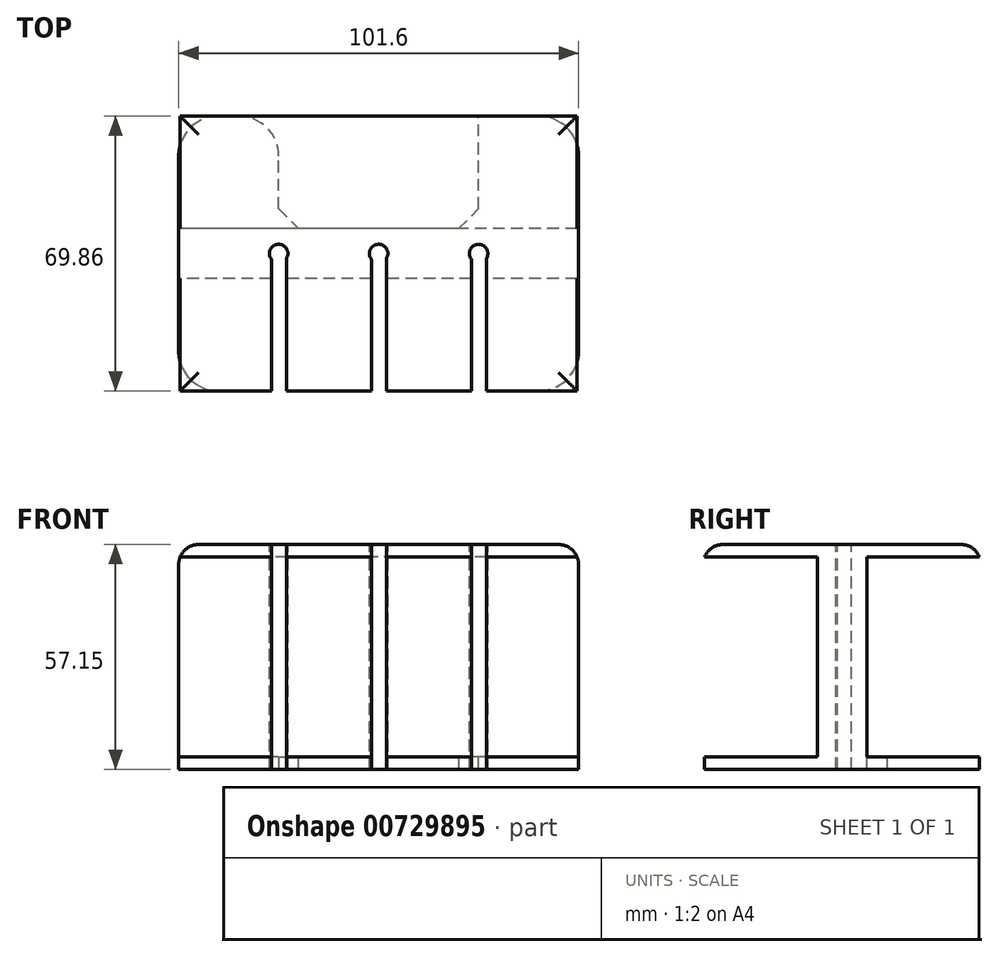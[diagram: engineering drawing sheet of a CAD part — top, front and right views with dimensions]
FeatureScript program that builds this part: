
annotation { "Feature Type Name" : "Feature", "Feature Type Description" : "" }
export const myFeature = defineFeature(function(context is Context, id is Id, definition is map)
    precondition{}
    {
        {
            var Q0;
            Q0=qCreatedBy(makeId("Right.planeOp"),FACE);
            var sketch = newSketch(context, id + "F0", { "sketchPlane" : qUnion([Q0])});
            skLineSegment(sketch, "E0.bottom", {"start": v(6.3, 28.58) * mm, "end": v(-6.3, 28.58) * mm});
            skLineSegment(sketch, "E0.top", {"start": v(6.3, -28.58) * mm, "end": v(-6.3, -28.58) * mm});
            skLineSegment(sketch, "E0.left", {"start": v(6.3, 28.58) * mm, "end": v(6.3, -28.58) * mm});
            skLineSegment(sketch, "E0.right", {"start": v(-6.3, 28.58) * mm, "end": v(-6.3, -28.58) * mm});
            skPoint(sketch, "E0.middle", {"position": v(0, 0) * mm});
            skLineSegment(sketch, "E1.bottom", {"start": v(0, 28.58) * mm, "end": v(-34.93, 28.58) * mm});
            skLineSegment(sketch, "E1.top", {"start": v(0, 25.4) * mm, "end": v(-34.93, 25.4) * mm});
            skLineSegment(sketch, "E1.left", {"start": v(0, 28.58) * mm, "end": v(0, 25.4) * mm});
            skLineSegment(sketch, "E1.right", {"start": v(-34.93, 28.57) * mm, "end": v(-34.93, 25.4) * mm});
            skLineSegment(sketch, "E2.MirrorCS", {"start": v(0, 28.58) * mm, "end": v(34.93, 28.58) * mm});
            skLineSegment(sketch, "E3.MirrorCS", {"start": v(0, 25.4) * mm, "end": v(34.93, 25.4) * mm});
            skLineSegment(sketch, "E4.MirrorCS", {"start": v(34.93, 28.58) * mm, "end": v(34.93, 25.4) * mm});
            skLineSegment(sketch, "E5.MirrorCS", {"start": v(0, -28.58) * mm, "end": v(-34.92, -28.58) * mm});
            skLineSegment(sketch, "E6.MirrorCS", {"start": v(0, -28.58) * mm, "end": v(34.93, -28.58) * mm});
            skLineSegment(sketch, "E7.MirrorCS", {"start": v(0, -25.4) * mm, "end": v(34.93, -25.4) * mm});
            skLineSegment(sketch, "E8.MirrorCS", {"start": v(0, -25.4) * mm, "end": v(-34.92, -25.4) * mm});
            skLineSegment(sketch, "E9.MirrorCS", {"start": v(-34.93, -28.58) * mm, "end": v(-34.93, -25.4) * mm});
            skLineSegment(sketch, "E10.MirrorCS", {"start": v(34.93, -28.58) * mm, "end": v(34.93, -25.4) * mm});
            skSolve(sketch);
        }
        {
            var Q0;
            Q0 = qSketchRegion(id + "F0", true);
            extrude(context, id + "F1", {"entities" : qUnion([Q0]), "endBound" : BoundingType.SYMMETRIC, "depth" : 101.6 * mm, "offsetDistance" : 25.4 * mm});
        }
        {
            var Q0;
            Q0=makeQuery(id+"F1.opExtrude","SWEPT_FACE",FACE,{"disambiguationData":[OSD([sQuery(id+"F0.wireOp",EDGE,"E1.bottom"),sQuery(id+"F0.wireOp",EDGE,"E2.MirrorCS")])]});
            fillet(context, id + "F2", {"entities" : qUnion([Q0]), "radius" : 5.08 * mm, "tangentPropagation" : true, "allowEdgeOverflow" : false});
        }
        {
            var Q0;
            Q0=makeQuery(id+"F1.opExtrude","SWEPT_FACE",FACE,{"disambiguationData":[OSD([sQuery(id+"F0.wireOp",EDGE,"E1.bottom"),sQuery(id+"F0.wireOp",EDGE,"E2.MirrorCS")])]});
            var sketch = newSketch(context, id + "F3", { "sketchPlane" : qUnion([Q0])});
            skCircle(sketch, "E11", {"center": v(0, 0) * mm, "radius": 2.35 * mm});
            skCircle(sketch, "E12", {"center": v(-25.4, 0) * mm, "radius": 2.35 * mm});
            skCircle(sketch, "E13", {"center": v(25.4, 0) * mm, "radius": 2.35 * mm});
            skLineSegment(sketch, "E14", {"start": v(-27.26, 0) * mm, "end": v(-27.26, -36.25) * mm});
            skLineSegment(sketch, "E15", {"start": v(-27.26, -36.25) * mm, "end": v(-23.45, -36.25) * mm});
            skLineSegment(sketch, "E16", {"start": v(-23.45, -36.25) * mm, "end": v(-23.45, 0) * mm});
            skLineSegment(sketch, "E17", {"start": v(-1.86, 0) * mm, "end": v(-1.86, -35.89) * mm});
            skLineSegment(sketch, "E18", {"start": v(-1.86, -35.89) * mm, "end": v(1.95, -35.89) * mm});
            skLineSegment(sketch, "E19", {"start": v(1.95, -35.89) * mm, "end": v(1.95, 0) * mm});
            skLineSegment(sketch, "E20", {"start": v(23.6, 0) * mm, "end": v(23.6, -37.47) * mm});
            skLineSegment(sketch, "E21", {"start": v(23.6, -37.47) * mm, "end": v(27.41, -37.47) * mm});
            skLineSegment(sketch, "E22", {"start": v(27.41, -37.47) * mm, "end": v(27.41, 0) * mm});
            skSolve(sketch);
        }
        {
            var Q0;
            Q0 = qSketchRegion(id + "F3", true);
            extrude(context, id + "F4", {"entities" : qUnion([Q0]), "operationType" : NewBodyOperationType.REMOVE, "endBound" : BoundingType.THROUGH_ALL, "oppositeDirection" : true, "depth" : 25.4 * mm, "offsetDistance" : 25.4 * mm});
        }
        {
            var Q0;
            Q0=makeQuery(id+"F1.opExtrude","SWEPT_FACE",FACE,{"disambiguationData":[OSD([sQuery(id+"F0.wireOp",EDGE,"E7.MirrorCS")])]});
            var sketch = newSketch(context, id + "F5", { "sketchPlane" : qUnion([Q0])});
            skLineSegment(sketch, "E23.bottom", {"start": v(-25.4, 6.3) * mm, "end": v(25.4, 6.3) * mm});
            skLineSegment(sketch, "E23.top", {"start": v(-25.4, 34.93) * mm, "end": v(25.4, 34.93) * mm});
            skLineSegment(sketch, "E23.left", {"start": v(-25.4, 6.3) * mm, "end": v(-25.4, 34.93) * mm});
            skLineSegment(sketch, "E23.right", {"start": v(25.4, 6.3) * mm, "end": v(25.4, 34.93) * mm});
            skSolve(sketch);
        }
        {
            var Q0;
            Q0 = qSketchRegion(id + "F5", true);
            extrude(context, id + "F6", {"entities" : qUnion([Q0]), "operationType" : NewBodyOperationType.REMOVE, "endBound" : BoundingType.THROUGH_ALL, "oppositeDirection" : true, "depth" : 25.4 * mm, "offsetDistance" : 25.4 * mm});
        }
        {
            var Q0;
            Q0=makeQuery(id+"F1.opExtrude","CAP_EDGE",EDGE,{"disambiguationData":[OSD([sQuery(id+"F0.wireOp",EDGE,"E10.MirrorCS")])],"isStart":false});
            var Q1;
            Q1=makeQuery(id+"F6.boolean.opBoolean","COPY",EDGE,{"derivedFrom":makeQuery(id+"F6.opExtrude","SWEPT_EDGE",EDGE,{"disambiguationData":[OSD([sQuery(id+"F0.wireOp",EDGE,"E7.MirrorCS"),sQuery(id+"F0.wireOp",EDGE,"E10.MirrorCS"),sQuery(id+"F5.wireOp",EDGE,"E23.top"),sQuery(id+"F5.wireOp",EDGE,"E23.right")])]})});
            var Q2;
            Q2=makeQuery(id+"F6.boolean.opBoolean","COPY",EDGE,{"derivedFrom":makeQuery(id+"F6.opExtrude","SWEPT_EDGE",EDGE,{"disambiguationData":[OSD([sQuery(id+"F0.wireOp",EDGE,"E7.MirrorCS"),sQuery(id+"F0.wireOp",EDGE,"E10.MirrorCS"),sQuery(id+"F5.wireOp",EDGE,"E23.top"),sQuery(id+"F5.wireOp",EDGE,"E23.left")])]})});
            var Q3;
            Q3=makeQuery(id+"F1.opExtrude","CAP_EDGE",EDGE,{"disambiguationData":[OSD([sQuery(id+"F0.wireOp",EDGE,"E10.MirrorCS")])],"isStart":true});
            var Q4;
            Q4=makeQuery(id+"F1.opExtrude","CAP_EDGE",EDGE,{"disambiguationData":[OSD([sQuery(id+"F0.wireOp",EDGE,"E9.MirrorCS")])],"isStart":true});
            var Q5;
            Q5=makeQuery(id+"F1.opExtrude","CAP_EDGE",EDGE,{"disambiguationData":[OSD([sQuery(id+"F0.wireOp",EDGE,"E9.MirrorCS")])],"isStart":false});
            fillet(context, id + "F7", {"entities" : qUnion([Q0, Q1, Q2, Q3, Q4, Q5]), "radius" : 10.16 * mm, "tangentPropagation" : true, "allowEdgeOverflow" : false});
        }
        {
            var Q0;
            Q0=makeQuery(id+"F6.boolean.opBoolean","COPY",EDGE,{"derivedFrom":makeQuery(id+"F6.opExtrude","SWEPT_EDGE",EDGE,{"disambiguationData":[OSD([sQuery(id+"F0.wireOp",EDGE,"E0.left"),sQuery(id+"F0.wireOp",EDGE,"E7.MirrorCS"),sQuery(id+"F5.wireOp",EDGE,"E23.bottom"),sQuery(id+"F5.wireOp",EDGE,"E23.left")])]})});
            var Q1;
            Q1=makeQuery(id+"F6.boolean.opBoolean","COPY",EDGE,{"derivedFrom":makeQuery(id+"F6.opExtrude","SWEPT_EDGE",EDGE,{"disambiguationData":[OSD([sQuery(id+"F0.wireOp",EDGE,"E0.left"),sQuery(id+"F0.wireOp",EDGE,"E7.MirrorCS"),sQuery(id+"F5.wireOp",EDGE,"E23.bottom"),sQuery(id+"F5.wireOp",EDGE,"E23.right")])]})});
            chamfer(context, id + "F8", {"entities" : qUnion([Q0, Q1]), "width" : 5.08 * mm, "tangentPropagation" : true});
        }
    });
